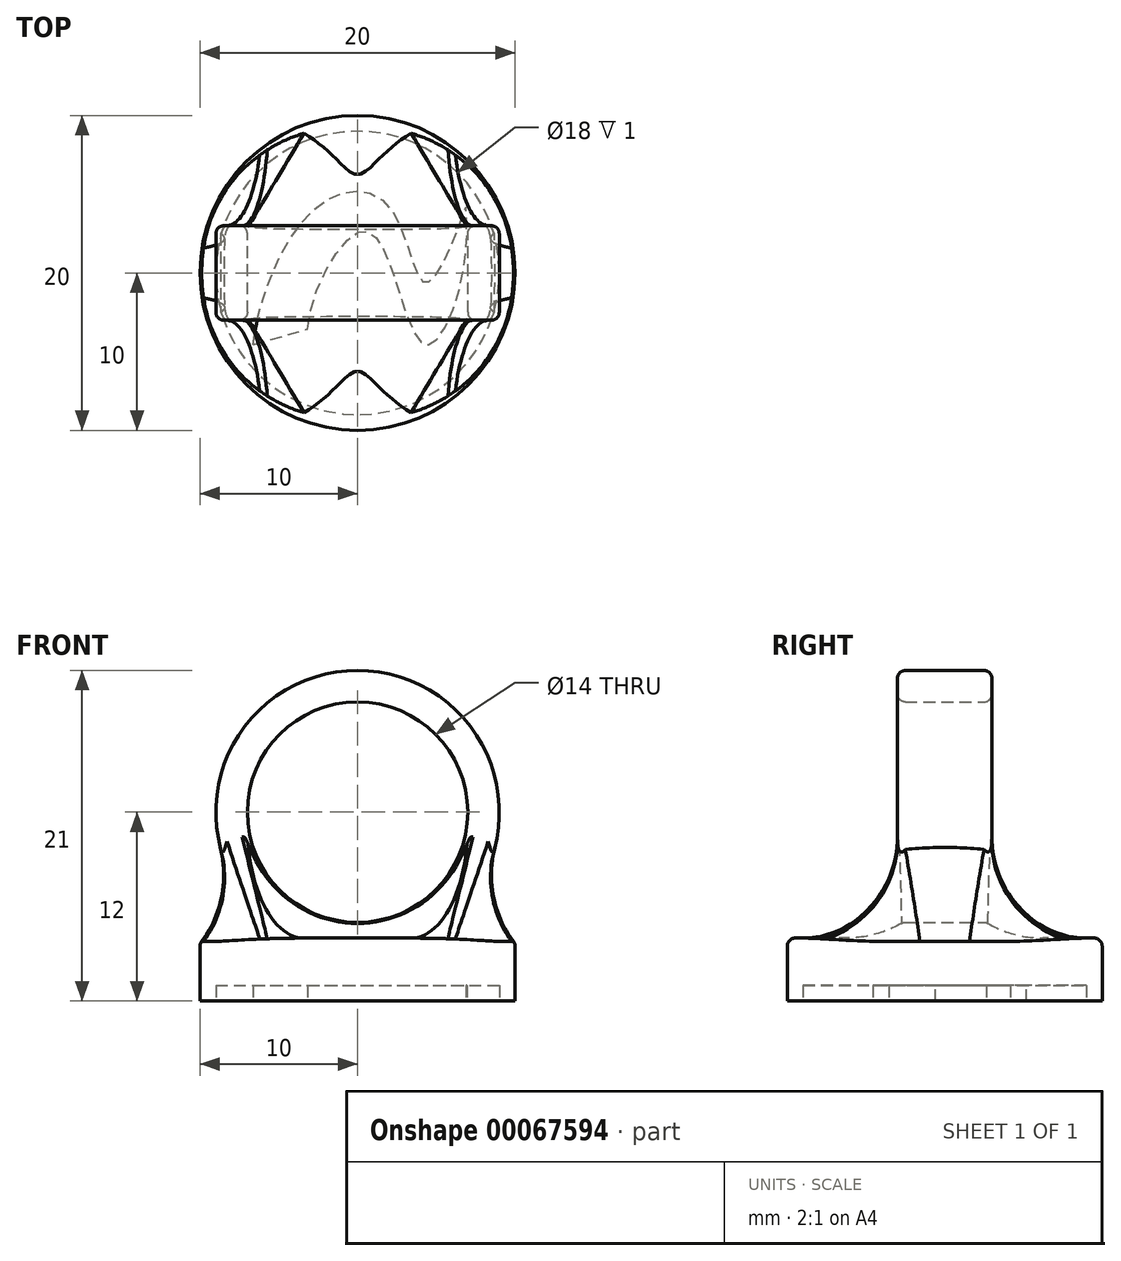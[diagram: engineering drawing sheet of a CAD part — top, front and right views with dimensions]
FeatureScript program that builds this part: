
annotation { "Feature Type Name" : "Feature", "Feature Type Description" : "" }
export const myFeature = defineFeature(function(context is Context, id is Id, definition is map)
    precondition{}
    {
        {
            var Q0;
            Q0=qCreatedBy(makeId("Front.planeOp"),FACE);
            var sketch = newSketch(context, id + "F0", { "sketchPlane" : qUnion([Q0])});
            skCircle(sketch, "E0", {"center": v(0, 0) * mm, "radius": 7 * mm});
            skCircle(sketch, "E1", {"center": v(0, 0) * mm, "radius": 9 * mm});
            skPoint(sketch, "E2", {"position": v(0, -9) * mm});
            skSolve(sketch);
        }
        {
            var Q0;
            Q0=makeQuery(id+"F0.imprint","IMPRINT",FACE,{"disambiguationData":[TD([[makeQuery(id+"F0.imprint","IMPRINT",EDGE,{"derivedFrom":sQuery(id+"F0.wireOp",EDGE,"E0")}),-1.0]])]});
            extrude(context, id + "F1", {"entities" : qUnion([Q0]), "endBound" : BoundingType.SYMMETRIC, "depth" : 6 * mm});
        }
        {
            var Q0;
            Q0=qCreatedBy(makeId("Top.planeOp"),FACE);
            var Q1;
            Q1=sQuery(id+"F0.wireOp",VERTEX,"E2");
            cPlane(context, id + "F2", {"entities" : qUnion([Q0, Q1]), "cplaneType" : CPlaneType.PLANE_POINT, "offset" : 150 * mm, "width" : 150 * mm, "height" : 150 * mm});
        }
        {
            var Q0;
            Q0=qCreatedBy(id+"F2.planeOp",FACE);
            var sketch = newSketch(context, id + "F3", { "sketchPlane" : qUnion([Q0])});
            skCircle(sketch, "E3", {"center": v(0, 0) * mm, "radius": 10 * mm});
            skSolve(sketch);
        }
        {
            var Q0;
            Q0=makeQuery(id+"F3.imprint","IMPRINT",FACE,{"disambiguationData":[TD([[makeQuery(id+"F3.imprint","IMPRINT",EDGE,{"derivedFrom":sQuery(id+"F3.wireOp",EDGE,"E3")}),1.0]])]});
            extrude(context, id + "F4", {"entities" : qUnion([Q0]), "operationType" : NewBodyOperationType.ADD, "oppositeDirection" : true, "depth" : 3 * mm, "hasSecondDirection" : true, "secondDirectionOppositeDirection" : false, "secondDirectionDepth" : 1 * mm});
        }
        {
            var Q0;
            Q0=makeQuery(id+"F1.opExtrude","CAP_EDGE",EDGE,{"disambiguationData":[OSD([sQuery(id+"F0.wireOp",EDGE,"E1")])],"isStart":true});
            var Q1;
            Q1=makeQuery(id+"F1.opExtrude","CAP_EDGE",EDGE,{"disambiguationData":[OSD([sQuery(id+"F0.wireOp",EDGE,"E1")])],"isStart":false});
            var Q2;
            Q2=makeQuery(id+"F1.opExtrude","CAP_EDGE",EDGE,{"disambiguationData":[OSD([sQuery(id+"F0.wireOp",EDGE,"E0")])],"isStart":true});
            var Q3;
            Q3=makeQuery(id+"F1.opExtrude","CAP_EDGE",EDGE,{"disambiguationData":[OSD([sQuery(id+"F0.wireOp",EDGE,"E0")])],"isStart":false});
            var Q4;
            Q4=makeQuery(id+"F4.opExtrude","CAP_EDGE",EDGE,{"disambiguationData":[OSD([sQuery(id+"F3.wireOp",EDGE,"E3")])],"isStart":true});
            fillet(context, id + "F5", {"entities" : qUnion([Q0, Q1, Q2, Q3, Q4]), "radius" : 0.5 * mm, "tangentPropagation" : true, "allowEdgeOverflow" : false});
        }
        {
            var Q0;
            Q0=makeQuery(id+"F4.boolean.opBoolean","INTERSECT",EDGE,{"derivedFrom":[makeQuery(id+"F1.opExtrude","CAP_FACE",FACE,{"disambiguationData":[OSD([sQuery(id+"F0.wireOp",EDGE,"E0"),sQuery(id+"F0.wireOp",EDGE,"E1")])],"isStart":true}),makeQuery(id+"F4.opExtrude","CAP_FACE",FACE,{"disambiguationData":[OSD([sQuery(id+"F3.wireOp",EDGE,"E3")])],"isStart":true})]});
            fillet(context, id + "F6", {"entities" : qUnion([Q0]), "radius" : 7 * mm, "tangentPropagation" : true, "allowEdgeOverflow" : false});
        }
        {
            var Q0;
            Q0=makeQuery(id+"F4.opExtrude","CAP_FACE",FACE,{"disambiguationData":[OSD([sQuery(id+"F3.wireOp",EDGE,"E3")])],"isStart":false});
            var sketch = newSketch(context, id + "F7", { "sketchPlane" : qUnion([Q0])});
            skFitSpline(sketch, "E4", {"points": [v(-6.63, 4.56) * mm, v(-2.26, -4.44) * mm, v(2, -4.2) * mm, v(4.24, 0.6) * mm, v(6.88, -4.19) * mm], "startDerivative": vector(3.58, -31.22) * mm, "endDerivative": vector(9.96, -28.96) * mm});
            skLineSegment(sketch, "E5", {"start": v(-6.63, 4.56) * mm, "end": v(-3.18, 3.56) * mm});
            skFitSpline(sketch, "E6", {"points": [v(-3.18, 3.56) * mm, v(0.21, -2.65) * mm, v(2.38, 0.4) * mm, v(4.45, 4.56) * mm, v(6.88, -4.19) * mm], "startDerivative": vector(1.14, -24.97) * mm, "endDerivative": vector(-4.3, -40.7) * mm});
            skCircle(sketch, "E7", {"center": v(0, 0) * mm, "radius": 9 * mm});
            skSolve(sketch);
        }
        {
            var Q0;
            Q0=makeQuery(id+"F7.imprint","IMPRINT",FACE,{"disambiguationData":[TD([[makeQuery(id+"F7.imprint","IMPRINT",EDGE,{"derivedFrom":sQuery(id+"F7.wireOp",EDGE,"E4")}),-1.0]])]});
            extrude(context, id + "F8", {"entities" : qUnion([Q0]), "operationType" : NewBodyOperationType.REMOVE, "oppositeDirection" : true, "depth" : 1 * mm});
        }
    });
